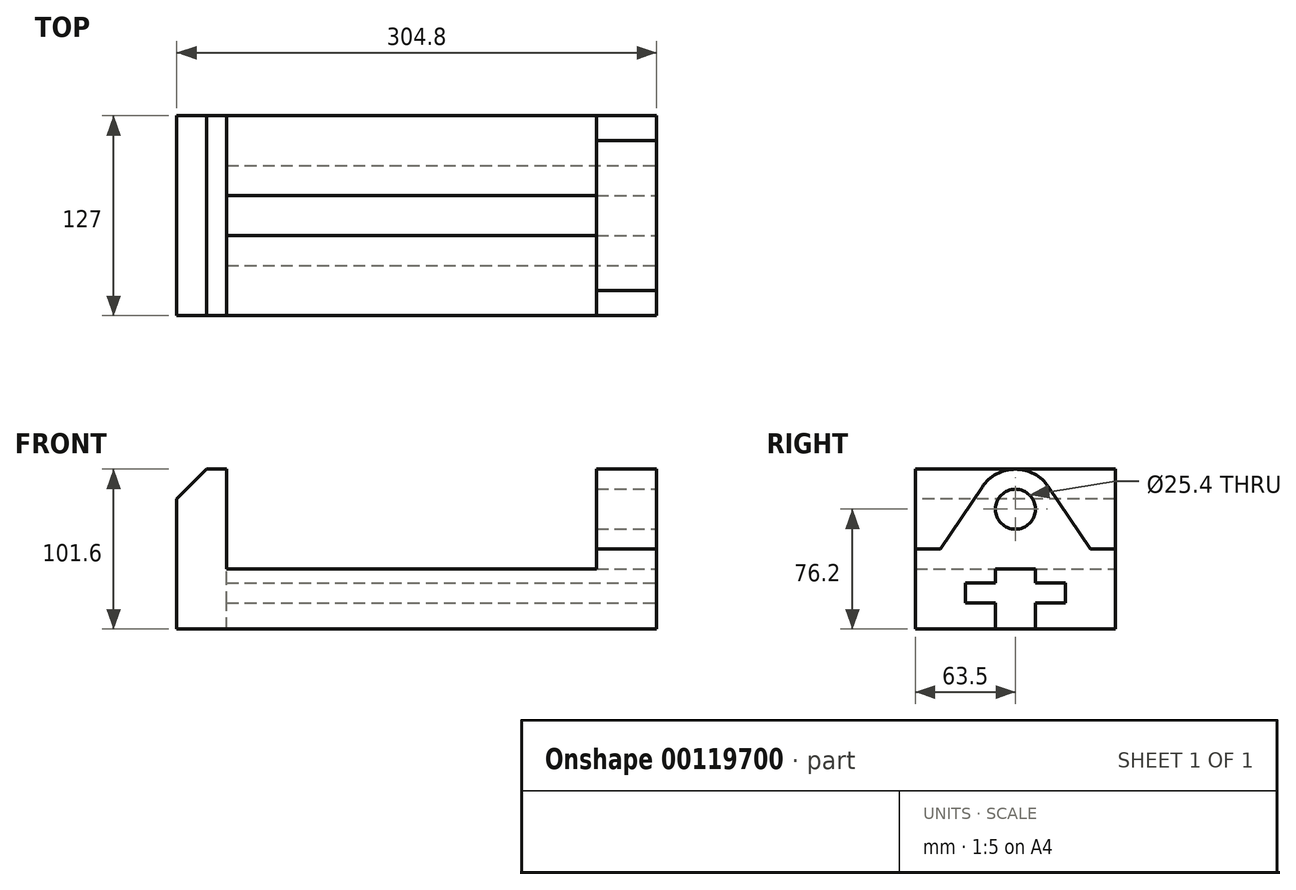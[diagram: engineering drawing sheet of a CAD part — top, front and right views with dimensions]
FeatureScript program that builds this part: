
annotation { "Feature Type Name" : "Feature", "Feature Type Description" : "" }
export const myFeature = defineFeature(function(context is Context, id is Id, definition is map)
    precondition{}
    {
        {
            var Q0;
            Q0=qCreatedBy(makeId("Front.planeOp"),FACE);
            var sketch = newSketch(context, id + "F0", { "sketchPlane" : qUnion([Q0])});
            skLineSegment(sketch, "E0", {"start": v(0, 0) * mm, "end": v(0, 101.6) * mm});
            skLineSegment(sketch, "E1", {"start": v(0, 101.6) * mm, "end": v(31.75, 101.6) * mm});
            skLineSegment(sketch, "E2", {"start": v(31.75, 101.6) * mm, "end": v(31.75, 38.1) * mm});
            skLineSegment(sketch, "E3", {"start": v(31.75, 38.1) * mm, "end": v(266.7, 38.1) * mm});
            skLineSegment(sketch, "E4", {"start": v(266.7, 38.1) * mm, "end": v(266.7, 101.6) * mm});
            skLineSegment(sketch, "E5", {"start": v(266.7, 101.6) * mm, "end": v(304.8, 101.6) * mm});
            skLineSegment(sketch, "E6", {"start": v(304.8, 101.6) * mm, "end": v(304.8, 0) * mm});
            skLineSegment(sketch, "E7", {"start": v(304.8, 0) * mm, "end": v(0, 0) * mm});
            skSolve(sketch);
        }
        {
            var Q0;
            Q0 = qSketchRegion(id + "F0", true);
            extrude(context, id + "F1", {"entities" : qUnion([Q0]), "depth" : 127 * mm});
        }
        {
            var Q0;
            Q0=makeQuery(id+"F1.opExtrude","SWEPT_FACE",FACE,{"disambiguationData":[OSD([sQuery(id+"F0.wireOp",EDGE,"E6")])]});
            var sketch = newSketch(context, id + "F2", { "sketchPlane" : qUnion([Q0])});
            skCircle(sketch, "E8", {"center": v(-63.5, 76.2) * mm, "radius": 12.7 * mm});
            skLineSegment(sketch, "E9", {"start": v(-111.12, 50.8) * mm, "end": v(-84.6, 90.35) * mm});
            skLineSegment(sketch, "E10", {"start": v(-15.87, 50.8) * mm, "end": v(-42.4, 90.35) * mm});
            skArc(sketch, "E11", {"start": v(-42.4, 90.35) * mm, "mid": v(-63.5, 101.6) * mm, "end": v(-84.6, 90.35) * mm});
            skLineSegment(sketch, "E12", {"start": v(-111.12, 50.8) * mm, "end": v(-127, 50.8) * mm});
            skLineSegment(sketch, "E13", {"start": v(-15.87, 50.8) * mm, "end": v(0, 50.8) * mm});
            skLineSegment(sketch, "E14", {"start": v(-63.5, 101.6) * mm, "end": v(-63.5, 0) * mm, "construction": true});
            skLineSegment(sketch, "E15", {"start": v(-127, 50.8) * mm, "end": v(-127, 101.6) * mm});
            skLineSegment(sketch, "E16", {"start": v(-127, 101.6) * mm, "end": v(0, 101.6) * mm});
            skLineSegment(sketch, "E17", {"start": v(0, 101.6) * mm, "end": v(0, 50.8) * mm});
            skLineSegment(sketch, "E18", {"start": v(-76.2, 0) * mm, "end": v(-76.2, 16.5) * mm});
            skLineSegment(sketch, "E19", {"start": v(-76.2, 16.5) * mm, "end": v(-95.25, 16.5) * mm});
            skLineSegment(sketch, "E20", {"start": v(-95.25, 16.5) * mm, "end": v(-95.25, 29.2) * mm});
            skLineSegment(sketch, "E21", {"start": v(-95.25, 29.2) * mm, "end": v(-76.2, 29.2) * mm});
            skLineSegment(sketch, "E22", {"start": v(-76.2, 29.2) * mm, "end": v(-76.2, 38.1) * mm});
            skLineSegment(sketch, "E23", {"start": v(-76.2, 38.1) * mm, "end": v(-50.8, 38.1) * mm});
            skLineSegment(sketch, "E24", {"start": v(-50.8, 38.1) * mm, "end": v(-50.8, 29.2) * mm});
            skLineSegment(sketch, "E25", {"start": v(-50.8, 29.2) * mm, "end": v(-31.75, 29.2) * mm});
            skLineSegment(sketch, "E26", {"start": v(-31.75, 29.2) * mm, "end": v(-31.75, 16.5) * mm});
            skLineSegment(sketch, "E27", {"start": v(-31.75, 16.5) * mm, "end": v(-50.8, 16.5) * mm});
            skLineSegment(sketch, "E28", {"start": v(-50.8, 16.5) * mm, "end": v(-50.8, 0) * mm});
            skLineSegment(sketch, "E29", {"start": v(-50.8, 0) * mm, "end": v(-76.2, 0) * mm});
            skSolve(sketch);
        }
        {
            var Q0;
            Q0 = qSketchRegion(id + "F2", true);
            extrude(context, id + "F3", {"entities" : qUnion([Q0]), "operationType" : NewBodyOperationType.REMOVE, "oppositeDirection" : true, "depth" : 273.05 * mm});
        }
        {
            var Q0;
            Q0=makeQuery(id+"F1.opExtrude","CAP_FACE",FACE,{"disambiguationData":[OSD([sQuery(id+"F0.wireOp",EDGE,"E0"),sQuery(id+"F0.wireOp",EDGE,"E1"),sQuery(id+"F0.wireOp",EDGE,"E2"),sQuery(id+"F0.wireOp",EDGE,"E3"),sQuery(id+"F0.wireOp",EDGE,"E4"),sQuery(id+"F0.wireOp",EDGE,"E5"),sQuery(id+"F0.wireOp",EDGE,"E6"),sQuery(id+"F0.wireOp",EDGE,"E7")])],"isStart":false});
            var sketch = newSketch(context, id + "F4", { "sketchPlane" : qUnion([Q0])});
            skLineSegment(sketch, "E30", {"start": v(0, 82.55) * mm, "end": v(19.05, 101.6) * mm});
            skLineSegment(sketch, "E31", {"start": v(0, 101.6) * mm, "end": v(0, 82.55) * mm});
            skLineSegment(sketch, "E32", {"start": v(0, 101.6) * mm, "end": v(19.05, 101.6) * mm});
            skSolve(sketch);
        }
        {
            var Q0;
            Q0 = qSketchRegion(id + "F4", true);
            extrude(context, id + "F5", {"entities" : qUnion([Q0]), "operationType" : NewBodyOperationType.REMOVE, "endBound" : BoundingType.THROUGH_ALL, "oppositeDirection" : true, "depth" : 25.4 * mm});
        }
    });
